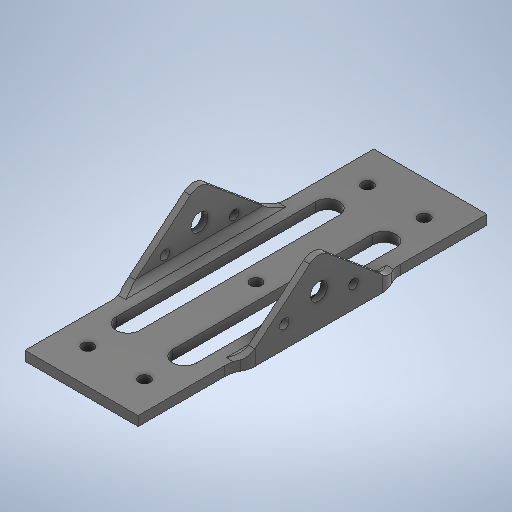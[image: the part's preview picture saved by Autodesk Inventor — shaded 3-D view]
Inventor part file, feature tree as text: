
AUTODESK INVENTOR PART (.ipt)
format: ipt  version: 2025.2 (Build 292293000, 293)  size: 524,800 bytes
history: native  units: mm
features: sketch x10, extrude x9, fillet x4, projected_geometry x2, plane x1, mirror x1
ambient origin geometry x8: Origin, YZ Plane, XZ Plane, XY Plane, X Axis, Y Axis, Z Axis, Center Point
bodies: Solid1 (feature_tree)
feature tree (27):
  extrude  "Extrusion1"  Depth=36.0mm
  extrude  "Extrusion2"  Depth=2.0mm TaperAngle=0.0deg
  sketch  "Sketch3"  dims[d11=90.0deg d20=50.0mm]
  plane  "Work Plane1"
  mirror  "Mirror1"
  extrude  "Extrusion3"  Depth=50.0mm
  extrude  "Extrusion4"  Depth=2.0mm
  extrude  "Extrusion5"  Depth=10.0mm
  fillet  "Fillet12"  Radius=7.5mm
  fillet  "Fillet13"  Radius=2.0mm
  fillet  "Fillet15"  Radius=10.0mm
  extrude  "Extrusion6"  Depth=6.88mm
  extrude  "Extrusion7"  Depth=2.0mm
  fillet  "Fillet16"  Radius=20.0mm
  extrude  "Extrusion8"  Depth=36.0mm
  extrude  "Extrusion9"  Depth=8.0mm
  sketch  "Sketch1"  dims[d0=36.0mm d1=71.0mm]
  sketch  "Sketch2"  dims[d2=2.0mm d3=0.0mm d9=2.0mm d10=0.0mm]
  sketch  "Sketch4"  dims[d21=2.0mm d26=5.0mm]
  sketch  "Sketch5"  dims[d27=9.0mm d28=5.0mm d32=7.5mm d33=2.0mm d34=0.0mm d37=10.0mm d38=0.0mm]
  projected_geometry  "Projected Loop1"
  sketch  "Sketch6"  dims[d61=6.88mm d62=6.88mm]
  sketch  "Sketch7"  dims[d63=2.0mm d64=2.0mm d65=20.0mm]
  sketch  "Sketch8"  dims[d66=36.0mm d67=20.0mm]
  sketch  "Sketch9"  dims[d68=0.0mm d69=0.0mm d70=8.0mm]
  sketch  "Sketch10"  dims[d71=8.0mm d73=3.75mm d74=3.6mm d75=3.6mm d76=3.6mm d77=3.6mm d78=3.6mm d79=2.0mm d80=0.0mm d81=5.4mm d82=0.0mm d83=0.0mm d84=2.0mm d85=3.0mm d86=3.0mm d87=0.0mm d88=0.0mm d89=1.0mm d90=0.0mm d15=0.5mm d16=0.872665mm d17=0.5mm d18=0.872665mm d53=0.5mm d54=0.872665mm d55=0.5mm d56=0.872665mm]
  projected_geometry  "Projected Loop2"
